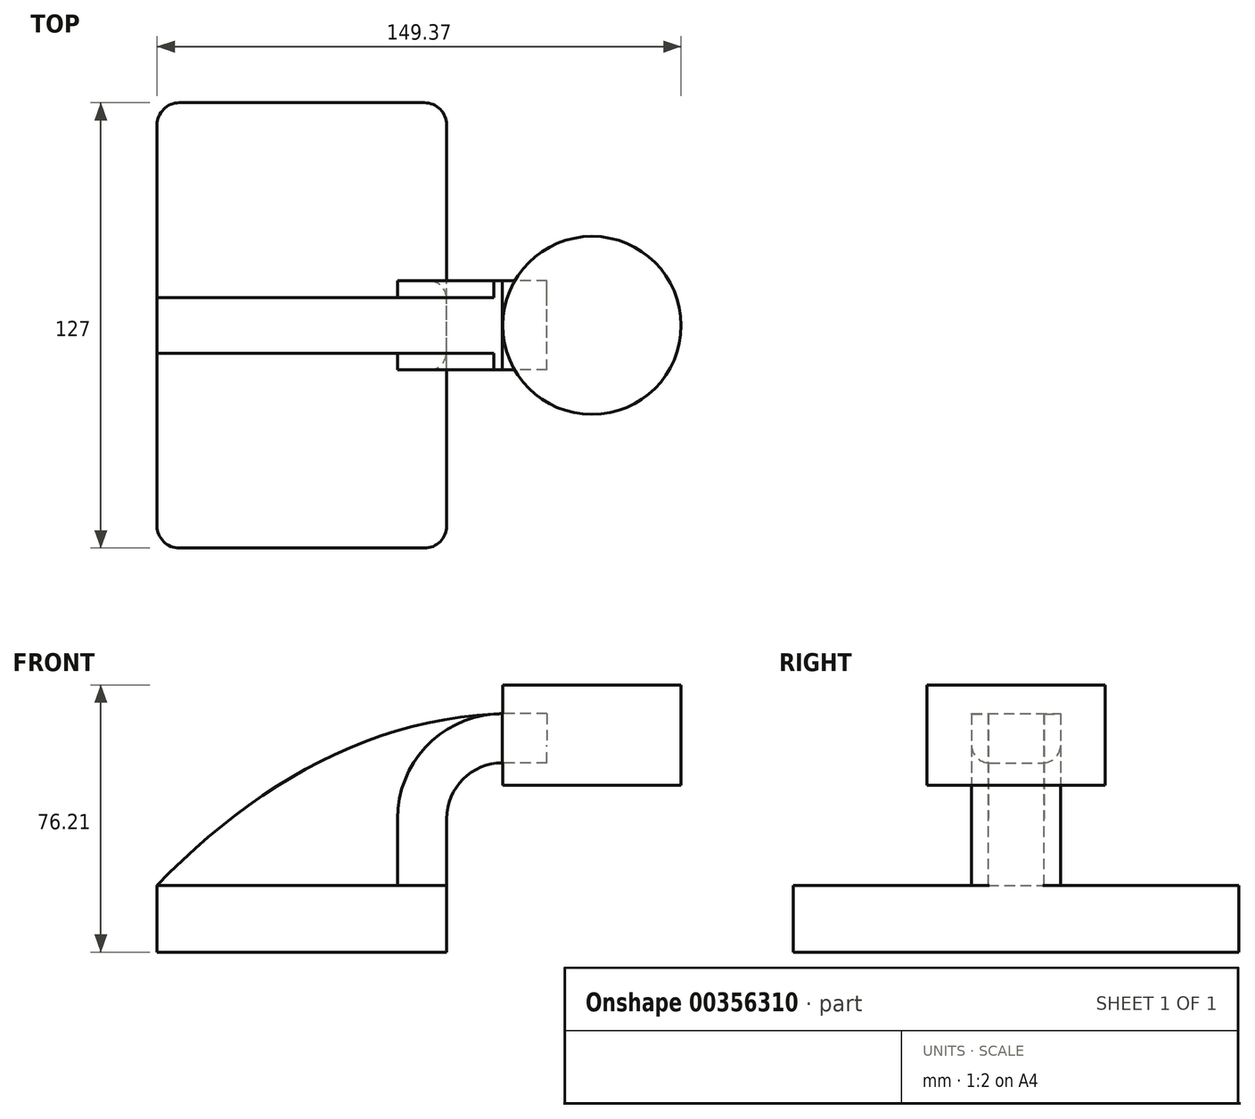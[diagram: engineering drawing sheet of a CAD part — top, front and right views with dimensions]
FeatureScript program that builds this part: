
annotation { "Feature Type Name" : "Feature", "Feature Type Description" : "" }
export const myFeature = defineFeature(function(context is Context, id is Id, definition is map)
    precondition{}
    {
        {
            var Q0;
            Q0=qCreatedBy(makeId("Front.planeOp"),FACE);
            var sketch = newSketch(context, id + "F0", { "sketchPlane" : qUnion([Q0])});
            skLineSegment(sketch, "E0.bottom", {"start": v(41.27, 9.53) * mm, "end": v(-41.28, 9.53) * mm});
            skLineSegment(sketch, "E0.top", {"start": v(41.28, -9.52) * mm, "end": v(-41.27, -9.52) * mm});
            skLineSegment(sketch, "E0.left", {"start": v(41.28, 9.53) * mm, "end": v(41.28, -9.52) * mm});
            skLineSegment(sketch, "E0.right", {"start": v(-41.28, 9.53) * mm, "end": v(-41.27, -9.52) * mm});
            skPoint(sketch, "E0.middle", {"position": v(0, 0) * mm});
            skLineSegment(sketch, "E1.bottom", {"start": v(107.95, 66.68) * mm, "end": v(57.15, 66.68) * mm});
            skLineSegment(sketch, "E1.top", {"start": v(107.95, 38.1) * mm, "end": v(57.15, 38.1) * mm});
            skLineSegment(sketch, "E1.left", {"start": v(107.95, 66.68) * mm, "end": v(107.95, 38.1) * mm});
            skLineSegment(sketch, "E1.right", {"start": v(57.15, 66.68) * mm, "end": v(57.15, 38.1) * mm});
            skPoint(sketch, "E1.middle", {"position": v(82.55, 52.39) * mm});
            skLineSegment(sketch, "E2", {"start": v(41.27, 9.53) * mm, "end": v(41.27, 28.58) * mm});
            skArc(sketch, "E3", {"start": v(41.27, 28.58) * mm, "mid": v(45.92, 39.8) * mm, "end": v(57.15, 44.45) * mm});
            skLineSegment(sketch, "E4", {"start": v(57.15, 44.45) * mm, "end": v(107.95, 44.45) * mm});
            skLineSegment(sketch, "E5.0", {"start": v(57.15, 58.45) * mm, "end": v(107.95, 58.45) * mm});
            skArc(sketch, "E5.1", {"start": v(27.27, 28.58) * mm, "mid": v(36.02, 49.7) * mm, "end": v(57.15, 58.45) * mm});
            skLineSegment(sketch, "E5.2", {"start": v(27.27, 9.53) * mm, "end": v(27.27, 28.58) * mm});
            skPoint(sketch, "E6", {"position": v(82.55, 58.45) * mm});
            skFitSpline(sketch, "E7", {"points": [v(-41.28, 9.52) * mm, v(57.15, 58.45) * mm], "startDerivative": vector(82.78, 85.94) * mm, "endDerivative": vector(112.88, 3.5) * mm});
            skSolve(sketch);
        }
        {
            var Q0;
            Q0=makeQuery(id+"F0.imprint","IMPRINT",FACE,{"disambiguationData":[TD([[makeQuery(id+"F0.imprint","IMPRINT",EDGE,{"derivedFrom":sQuery(id+"F0.wireOp",EDGE,"E0.top")}),-1.0]])]});
            extrude(context, id + "F1", {"entities" : qUnion([Q0]), "endBound" : BoundingType.SYMMETRIC, "depth" : 127 * mm});
        }
        {
            var Q0;
            {var subQ1=sQuery(id+"F0.wireOp",EDGE,"E2");Q0=makeQuery(id+"F0.imprint","IMPRINT",FACE,{"disambiguationData":[TD([[makeQuery(id+"F0.imprint","IMPRINT",EDGE,{"derivedFrom":subQ1}),1.0]])]});}
            extrude(context, id + "F2", {"entities" : qUnion([Q0]), "operationType" : NewBodyOperationType.ADD, "endBound" : BoundingType.SYMMETRIC, "depth" : 25.4 * mm});
        }
        {
            var Q0;
            {var subQ3=sQuery(id+"F0.wireOp",EDGE,"E5.2");Q0=makeQuery(id+"F0.imprint","IMPRINT",FACE,{"disambiguationData":[TD([[makeQuery(id+"F0.imprint","IMPRINT",EDGE,{"derivedFrom":subQ3}),1.0]])]});}
            extrude(context, id + "F3", {"entities" : qUnion([Q0]), "operationType" : NewBodyOperationType.ADD, "endBound" : BoundingType.SYMMETRIC, "depth" : 15.88 * mm});
        }
        {
            var Q0;
            Q0=qCreatedBy(makeId("Front.planeOp"),FACE);
            var sketch = newSketch(context, id + "F4", { "sketchPlane" : qUnion([Q0])});
            skLineSegment(sketch, "E8", {"start": v(82.55, 37.96) * mm, "end": v(82.55, 66.81) * mm});
            skSolve(sketch);
        }
        {
            var Q0;
            Q0=makeQuery(id+"F1.opExtrude","CAP_EDGE",EDGE,{"disambiguationData":[OSD([sQuery(id+"F0.wireOp",EDGE,"E0.left")])],"isStart":false});
            fillet(context, id + "F5", {"entities" : qUnion([Q0]), "radius" : 6.35 * mm, "tangentPropagation" : true, "allowEdgeOverflow" : false});
        }
        {
            var Q0;
            Q0=qCreatedBy(makeId("Front.planeOp"),FACE);
            var sketch = newSketch(context, id + "F6", { "sketchPlane" : qUnion([Q0])});
            skLineSegment(sketch, "E9.bottom", {"start": v(108.09, 38.1) * mm, "end": v(82.69, 38.1) * mm});
            skLineSegment(sketch, "E9.top", {"start": v(108.09, 66.68) * mm, "end": v(82.69, 66.68) * mm});
            skLineSegment(sketch, "E9.left", {"start": v(108.09, 38.1) * mm, "end": v(108.09, 66.68) * mm});
            skLineSegment(sketch, "E9.right", {"start": v(82.69, 38.1) * mm, "end": v(82.69, 66.68) * mm});
            skSolve(sketch);
        }
        {
            var Q0;
            Q0=makeQuery(id+"F6.imprint","IMPRINT",FACE,{"disambiguationData":[TD([[makeQuery(id+"F6.imprint","IMPRINT",EDGE,{"derivedFrom":sQuery(id+"F6.wireOp",EDGE,"E9.bottom")}),-1.0]])]});
            var Q1;
            Q1=sQuery(id+"F6.wireOp",EDGE,"E9.right");
            revolve(context, id + "F7", {"entities" : qUnion([Q0]), "axis" : qUnion([Q1]), "revolveType" : RevolveType.FULL});
        }
        {
            var Q0;
            Q0=makeQuery(id+"F1.opExtrude","CAP_EDGE",EDGE,{"disambiguationData":[OSD([sQuery(id+"F0.wireOp",EDGE,"E0.right")])],"isStart":false});
            fillet(context, id + "F8", {"entities" : qUnion([Q0]), "radius" : 6.35 * mm, "tangentPropagation" : true, "allowEdgeOverflow" : false});
        }
        {
            var Q0;
            Q0=makeQuery(id+"F1.opExtrude","CAP_EDGE",EDGE,{"disambiguationData":[OSD([sQuery(id+"F0.wireOp",EDGE,"E0.left")])],"isStart":true});
            var Q1;
            Q1=makeQuery(id+"F1.opExtrude","CAP_EDGE",EDGE,{"disambiguationData":[OSD([sQuery(id+"F0.wireOp",EDGE,"E0.right")])],"isStart":true});
            fillet(context, id + "F9", {"entities" : qUnion([Q0, Q1]), "radius" : 6.35 * mm, "tangentPropagation" : true, "allowEdgeOverflow" : false});
        }
        {
            var Q0;
            Q0=makeQuery(id+"F2.opExtrude","CAP_EDGE",EDGE,{"disambiguationData":[OSD([sQuery(id+"F0.wireOp",EDGE,"E3")])],"isStart":false});
            var Q1;
            Q1=makeQuery(id+"F2.opExtrude","CAP_EDGE",EDGE,{"disambiguationData":[OSD([sQuery(id+"F0.wireOp",EDGE,"E2")])],"isStart":true});
            fillet(context, id + "F10", {"entities" : qUnion([Q0, Q1]), "radius" : 5.08 * mm, "tangentPropagation" : true, "allowEdgeOverflow" : false});
        }
        {
            var Q0;
            Q0=makeQuery(id+"F2.opExtrude","SWEPT_FACE",FACE,{"disambiguationData":[OSD([sQuery(id+"F0.wireOp",EDGE,"E1.right")])]});
            extrude(context, id + "F11", {"entities" : qUnion([Q0]), "depth" : 12.7 * mm});
        }
    });
